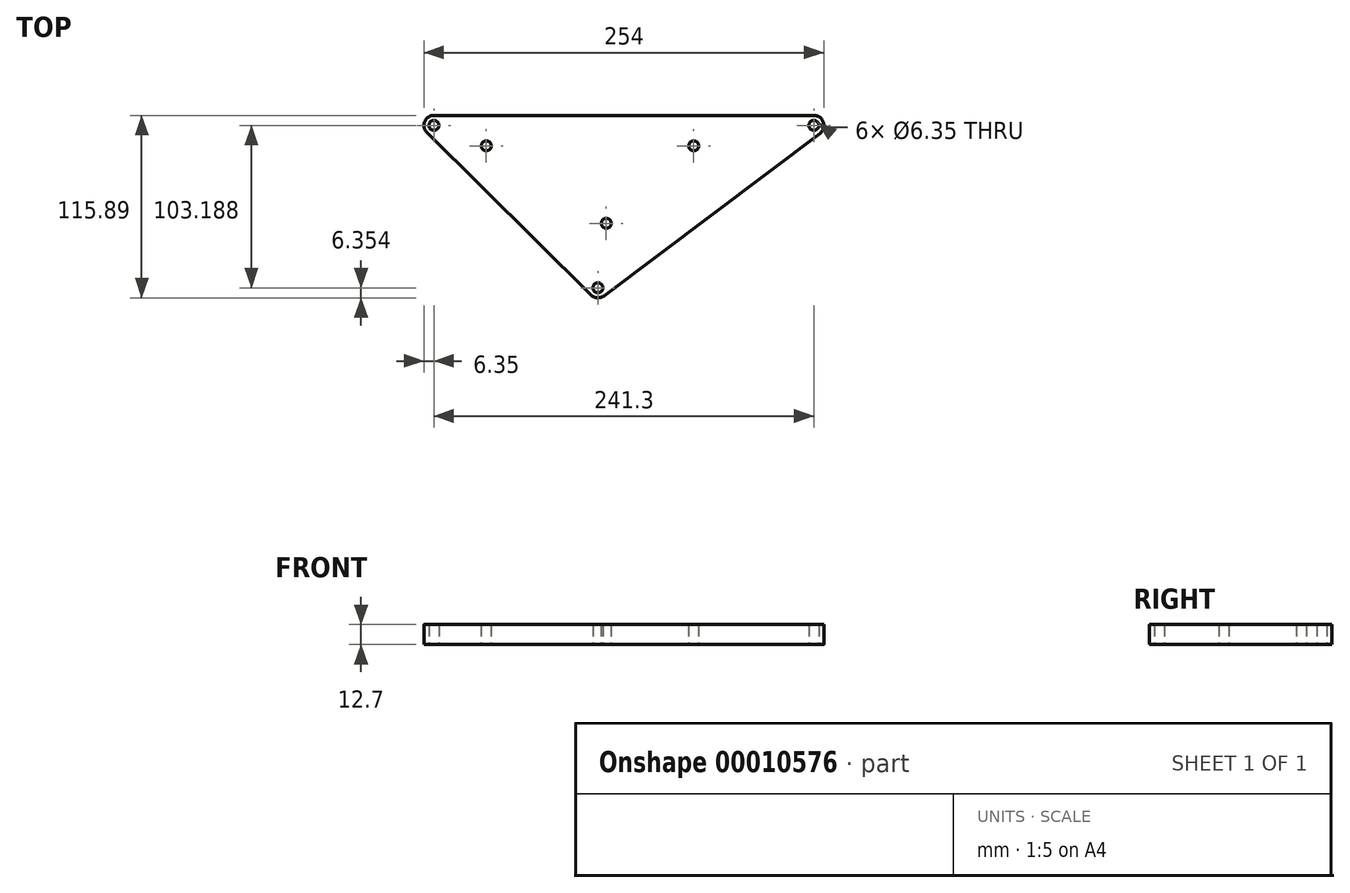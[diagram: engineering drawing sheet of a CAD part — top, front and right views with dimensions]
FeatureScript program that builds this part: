
annotation { "Feature Type Name" : "Feature", "Feature Type Description" : "" }
export const myFeature = defineFeature(function(context is Context, id is Id, definition is map)
    precondition{}
    {
        {
            var Q0;
            Q0=qCreatedBy(makeId("Top.planeOp"),FACE);
            var sketch = newSketch(context, id + "F0", { "sketchPlane" : qUnion([Q0])});
            skLineSegment(sketch, "E0", {"start": v(-104.14, 62.22) * mm, "end": v(137.16, 62.22) * mm, "construction": true});
            skLineSegment(sketch, "E1", {"start": v(0, 62.22) * mm, "end": v(0, -40.97) * mm, "construction": true});
            skLineSegment(sketch, "E2", {"start": v(-104.14, 62.22) * mm, "end": v(0, -40.97) * mm, "construction": true});
            skLineSegment(sketch, "E3", {"start": v(137.16, 62.22) * mm, "end": v(0, -40.97) * mm, "construction": true});
            skLineSegment(sketch, "E4.0", {"start": v(-104.14, 68.57) * mm, "end": v(137.16, 68.57) * mm});
            skLineSegment(sketch, "E4.1", {"start": v(-108.6, 57.71) * mm, "end": v(-4.47, -45.48) * mm});
            skLineSegment(sketch, "E4.2", {"start": v(140.98, 57.15) * mm, "end": v(3.82, -46.04) * mm});
            skPoint(sketch, "E5.visualSharp", {"position": v(-119.57, 68.57) * mm});
            skArc(sketch, "E5.filletArc", {"start": v(-104.14, 68.57) * mm, "mid": v(-110.01, 64.64) * mm, "end": v(-108.6, 57.71) * mm});
            skPoint(sketch, "E6.visualSharp", {"position": v(156.16, 68.57) * mm});
            skArc(sketch, "E6.filletArc", {"start": v(140.98, 57.15) * mm, "mid": v(143.18, 64.23) * mm, "end": v(137.16, 68.57) * mm});
            skPoint(sketch, "E7.visualSharp", {"position": v(-0.57, -49.34) * mm});
            skArc(sketch, "E7.filletArc", {"start": v(-4.47, -45.48) * mm, "mid": v(-0.43, -47.3) * mm, "end": v(3.82, -46.04) * mm});
            skCircle(sketch, "E8", {"center": v(-104.14, 62.22) * mm, "radius": 3.18 * mm});
            skCircle(sketch, "E9", {"center": v(0, -40.97) * mm, "radius": 3.18 * mm});
            skCircle(sketch, "E10", {"center": v(137.16, 62.22) * mm, "radius": 3.18 * mm});
            skLineSegment(sketch, "E11", {"start": v(-70.9, 49.2) * mm, "end": v(60.86, 49.2) * mm, "construction": true});
            skLineSegment(sketch, "E12", {"start": v(5.3, 49.2) * mm, "end": v(5.3, 0) * mm, "construction": true});
            skCircle(sketch, "E13", {"center": v(-70.9, 49.2) * mm, "radius": 3.18 * mm});
            skCircle(sketch, "E14", {"center": v(60.86, 49.2) * mm, "radius": 3.18 * mm});
            skCircle(sketch, "E15", {"center": v(5.3, 0) * mm, "radius": 3.17 * mm});
            skLineSegment(sketch, "E16", {"start": v(60.86, 49.2) * mm, "end": v(60.86, 68.57) * mm, "construction": true});
            skSolve(sketch);
        }
        {
            var Q0;
            Q0 = qSketchRegion(id + "F0", true);
            extrude(context, id + "F1", {"entities" : qUnion([Q0]), "depth" : 12.7 * mm});
        }
    });
